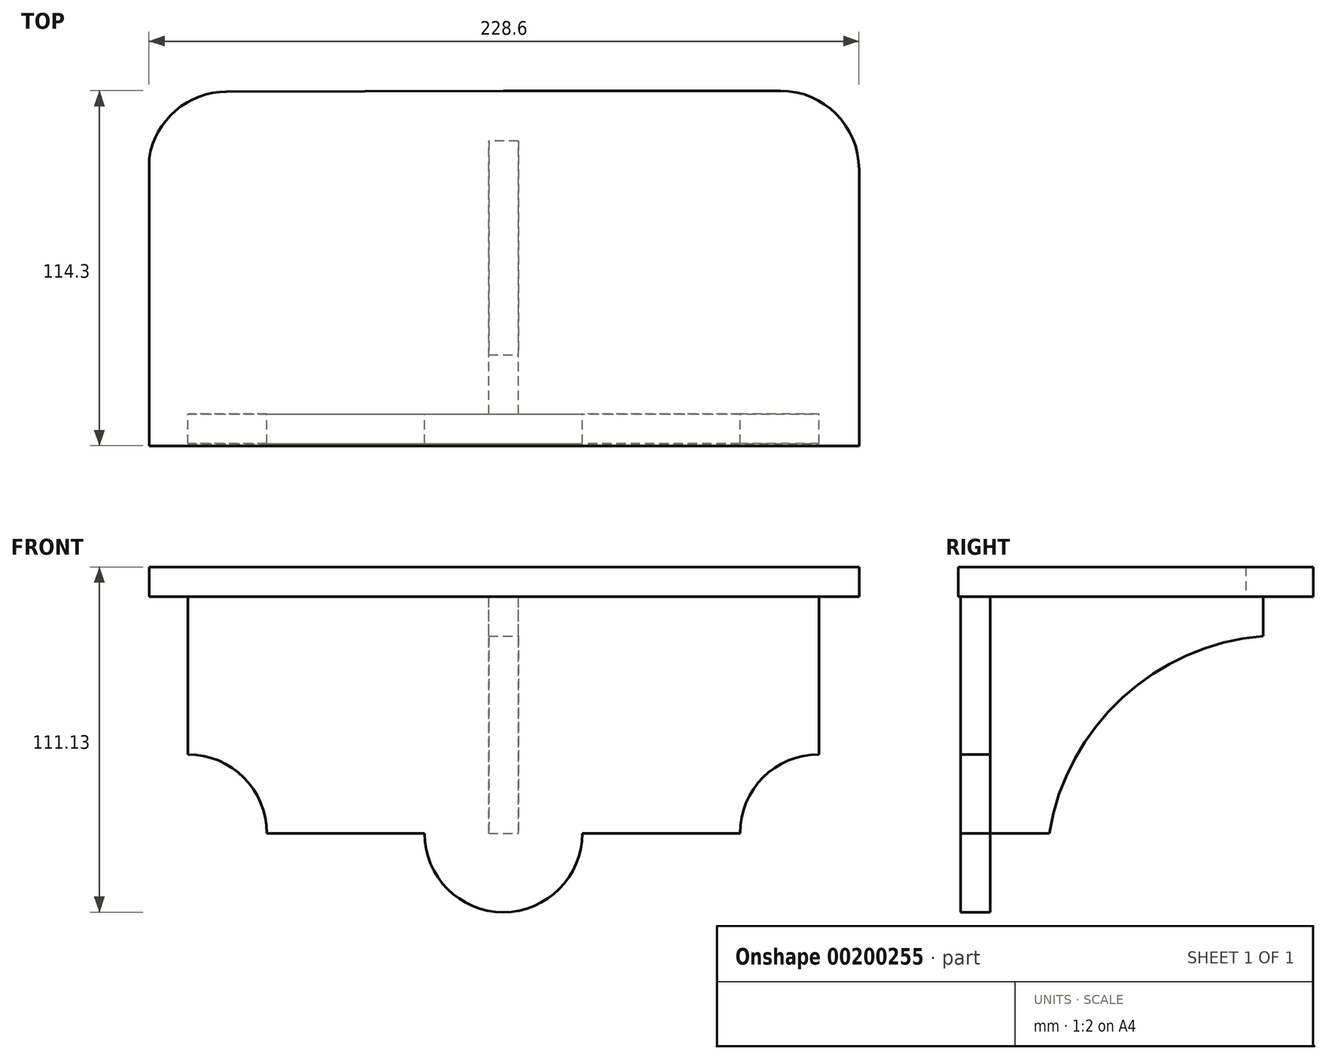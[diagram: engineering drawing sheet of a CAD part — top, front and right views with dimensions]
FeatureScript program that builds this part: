
annotation { "Feature Type Name" : "Feature", "Feature Type Description" : "" }
export const myFeature = defineFeature(function(context is Context, id is Id, definition is map)
    precondition{}
    {
        {
            var Q0;
            Q0=qCreatedBy(makeId("Top.planeOp"),FACE);
            var sketch = newSketch(context, id + "F0", { "sketchPlane" : qUnion([Q0])});
            skLineSegment(sketch, "E0.bottom", {"start": v(0, 59.94) * mm, "end": v(89.1, 59.94) * mm});
            skLineSegment(sketch, "E0.top", {"start": v(-114.1, -54.36) * mm, "end": v(114.5, -54.36) * mm});
            skLineSegment(sketch, "E0.left", {"start": v(-114.1, 38.2) * mm, "end": v(-114.1, -54.36) * mm});
            skLineSegment(sketch, "E0.right", {"start": v(114.5, 34.54) * mm, "end": v(114.5, -54.36) * mm});
            skArc(sketch, "E1", {"start": v(114.5, 34.54) * mm, "mid": v(107.06, 52.5) * mm, "end": v(89.1, 59.94) * mm});
            skLineSegment(sketch, "E2", {"start": v(-114.1, -54.36) * mm, "end": v(0.2, -54.36) * mm});
            skLineSegment(sketch, "E3", {"start": v(0.2, -54.36) * mm, "end": v(0, 59.94) * mm});
            skArc(sketch, "E4.MirrorCS", {"start": v(-114.41, 34.13) * mm, "mid": v(-107.04, 52.12) * mm, "end": v(-89.1, 59.62) * mm});
            skPoint(sketch, "E5", {"position": v(-89.1, 59.62) * mm});
            skLineSegment(sketch, "E6", {"start": v(-89.1, 59.62) * mm, "end": v(0, 59.94) * mm});
            skSolve(sketch);
        }
        {
            var Q0;
            {var subQ1=sQuery(id+"F0.wireOp",EDGE,"E0.left");Q0=makeQuery(id+"F0.imprint","IMPRINT",FACE,{"disambiguationData":[TD([[makeQuery(id+"F0.imprint","IMPRINT",EDGE,{"derivedFrom":subQ1}),1.0]])]});}
            var Q1;
            Q1=makeQuery(id+"F0.imprint","IMPRINT",FACE,{"disambiguationData":[TD([[makeQuery(id+"F0.imprint","IMPRINT",EDGE,{"derivedFrom":sQuery(id+"F0.wireOp",EDGE,"E0.bottom")}),-1.0]])]});
            extrude(context, id + "F1", {"entities" : qUnion([Q0, Q1]), "depth" : 9.52 * mm});
        }
        {
            var Q0;
            Q0=makeQuery(id+"F1.opExtrude","CAP_FACE",FACE,{"disambiguationData":[OSD([sQuery(id+"F0.wireOp",EDGE,"E0.bottom"),sQuery(id+"F0.wireOp",EDGE,"E0.top"),sQuery(id+"F0.wireOp",EDGE,"E0.left"),sQuery(id+"F0.wireOp",EDGE,"E0.right"),sQuery(id+"F0.wireOp",EDGE,"E1"),sQuery(id+"F0.wireOp",EDGE,"E2"),sQuery(id+"F0.wireOp",EDGE,"E4.MirrorCS"),sQuery(id+"F0.wireOp",EDGE,"E6")])],"isStart":true});
            var sketch = newSketch(context, id + "F2", { "sketchPlane" : qUnion([Q0])});
            skLineSegment(sketch, "E7", {"start": v(-8.24, 54.36) * mm, "end": v(-8.24, -34.54) * mm});
            skSolve(sketch);
        }
        {
            var Q0;
            Q0=makeQuery(id+"F2.imprint","IMPRINT",FACE,{"disambiguationData":[TD([[makeQuery(id+"F2.imprint","IMPRINT",EDGE,{"derivedFrom":makeQuery(id+"F1.opExtrude","CAP_EDGE",EDGE,{"disambiguationData":[OSD([sQuery(id+"F0.wireOp",EDGE,"E0.bottom")])],"isStart":true})}),1.0]])]});
            var sketch = newSketch(context, id + "F3", { "sketchPlane" : qUnion([Q0])});
            skLineSegment(sketch, "E8", {"start": v(-8.86, 53.72) * mm, "end": v(-8.86, 44.2) * mm});
            skLineSegment(sketch, "E9", {"start": v(-114.26, 54.66) * mm, "end": v(0.04, 54.66) * mm});
            skLineSegment(sketch, "E10", {"start": v(-114.26, 54.66) * mm, "end": v(-101.56, 54.66) * mm});
            skLineSegment(sketch, "E11", {"start": v(-101.56, 54.66) * mm, "end": v(-101.56, 44.66) * mm});
            skLineSegment(sketch, "E12", {"start": v(-8.86, 44.2) * mm, "end": v(-101.56, 44.2) * mm});
            skLineSegment(sketch, "E13.0", {"start": v(-114.1, 54.36) * mm, "end": v(114.5, 54.36) * mm});
            skLineSegment(sketch, "E14", {"start": v(0.04, 54.66) * mm, "end": v(0.04, 54.36) * mm});
            skLineSegment(sketch, "E15.0", {"start": v(-4.72, 54.66) * mm, "end": v(-4.72, 54.36) * mm});
            skLineSegment(sketch, "E16.0", {"start": v(4.8, 54.66) * mm, "end": v(4.8, 54.36) * mm});
            skLineSegment(sketch, "E17", {"start": v(4.8, -34.24) * mm, "end": v(4.8, -43.76) * mm});
            skLineSegment(sketch, "E18", {"start": v(4.8, -43.76) * mm, "end": v(-4.72, -43.76) * mm});
            skLineSegment(sketch, "E19", {"start": v(-4.72, -43.76) * mm, "end": v(-4.72, -34.24) * mm});
            skLineSegment(sketch, "E20", {"start": v(-8.86, 44.2) * mm, "end": v(4.8, 44.2) * mm});
            skLineSegment(sketch, "E21.trimOffspring", {"start": v(0.04, 44.2) * mm, "end": v(0.04, -43.76) * mm});
            skLineSegment(sketch, "E22.trimOffspring", {"start": v(4.8, 44.2) * mm, "end": v(4.8, -34.24) * mm});
            skLineSegment(sketch, "E23.trimOffspring", {"start": v(-4.72, 44.2) * mm, "end": v(-4.72, -34.24) * mm});
            skSolve(sketch);
        }
        {
            var Q0;
            {var subQ4=sQuery(id+"F3.wireOp",EDGE,"E17");Q0=makeQuery(id+"F3.imprint","IMPRINT",FACE,{"disambiguationData":[TD([[makeQuery(id+"F3.imprint","IMPRINT",EDGE,{"derivedFrom":subQ4}),-1.0]])]});}
            var Q1;
            {var subQ1=sQuery(id+"F3.wireOp",EDGE,"E19");Q1=makeQuery(id+"F3.imprint","IMPRINT",FACE,{"disambiguationData":[TD([[makeQuery(id+"F3.imprint","IMPRINT",EDGE,{"derivedFrom":subQ1}),-1.0]])]});}
            extrude(context, id + "F4", {"entities" : qUnion([Q0, Q1]), "operationType" : NewBodyOperationType.ADD, "depth" : 76.2 * mm});
        }
        {
            var Q0;
            Q0=makeQuery(id+"F4.opExtrude","SWEPT_FACE",FACE,{"disambiguationData":[OSD([sQuery(id+"F3.wireOp",EDGE,"E20")])]});
            var sketch = newSketch(context, id + "F5", { "sketchPlane" : qUnion([Q0])});
            skLineSegment(sketch, "E24", {"start": v(-114.32, 0) * mm, "end": v(-101.62, 0) * mm});
            skLineSegment(sketch, "E25", {"start": v(-101.62, 0) * mm, "end": v(-101.62, -50.8) * mm});
            skLineSegment(sketch, "E26", {"start": v(114.28, 0) * mm, "end": v(101.58, 0) * mm});
            skLineSegment(sketch, "E27", {"start": v(101.58, 0) * mm, "end": v(101.58, -50.8) * mm});
            skLineSegment(sketch, "E28", {"start": v(-76.22, -76.2) * mm, "end": v(-25.42, -76.2) * mm});
            skArc(sketch, "E29", {"start": v(-76.22, -76.2) * mm, "mid": v(-83.66, -58.24) * mm, "end": v(-101.62, -50.8) * mm});
            skArc(sketch, "E30", {"start": v(101.58, -50.8) * mm, "mid": v(83.61, -58.24) * mm, "end": v(76.18, -76.2) * mm});
            skLineSegment(sketch, "E31", {"start": v(76.18, -76.2) * mm, "end": v(25.38, -76.2) * mm});
            skArc(sketch, "E32", {"start": v(-25.42, -76.2) * mm, "mid": v(-0.02, -101.6) * mm, "end": v(25.38, -76.2) * mm});
            skLineSegment(sketch, "E33.trimOffspring", {"start": v(25.38, -76.2) * mm, "end": v(76.18, -76.2) * mm});
            skLineSegment(sketch, "E34", {"start": v(-101.62, 0) * mm, "end": v(101.58, 0) * mm});
            skSolve(sketch);
        }
        {
            var Q0;
            Q0 = qSketchRegion(id + "F5", true);
            extrude(context, id + "F6", {"entities" : qUnion([Q0]), "depth" : 9.52 * mm});
        }
        {
            var Q0;
            Q0 = qSketchRegion(id + "F5", true);
            extrude(context, id + "F7", {"entities" : qUnion([Q0]), "operationType" : NewBodyOperationType.ADD, "depth" : 9.52 * mm});
        }
        {
            var Q0;
            Q0=makeQuery(id+"F4.opExtrude","SWEPT_FACE",FACE,{"disambiguationData":[OSD([sQuery(id+"F3.wireOp",EDGE,"E17"),sQuery(id+"F3.wireOp",EDGE,"E22.trimOffspring")])]});
            var sketch = newSketch(context, id + "F8", { "sketchPlane" : qUnion([Q0])});
            skPoint(sketch, "E35", {"position": v(43.76, -76.2) * mm});
            skLineSegment(sketch, "E36", {"start": v(43.76, 0) * mm, "end": v(43.76, -12.7) * mm});
            skLineSegment(sketch, "E37", {"start": v(-44.2, -76.2) * mm, "end": v(-25.14, -76.2) * mm});
            skArc(sketch, "E38", {"start": v(43.76, -12.7) * mm, "mid": v(-1.6, -32.6) * mm, "end": v(-25.14, -76.2) * mm});
            skSolve(sketch);
        }
        {
            var Q0;
            {var subQ0=sQuery(id+"F8.wireOp",EDGE,"E38");Q0=makeQuery(id+"F8.imprint","IMPRINT",FACE,{"disambiguationData":[TD([[makeQuery(id+"F8.imprint","IMPRINT",EDGE,{"derivedFrom":subQ0}),1.0]])]});}
            extrude(context, id + "F9", {"entities" : qUnion([Q0]), "operationType" : NewBodyOperationType.REMOVE, "oppositeDirection" : true, "depth" : 25.4 * mm});
        }
    });
